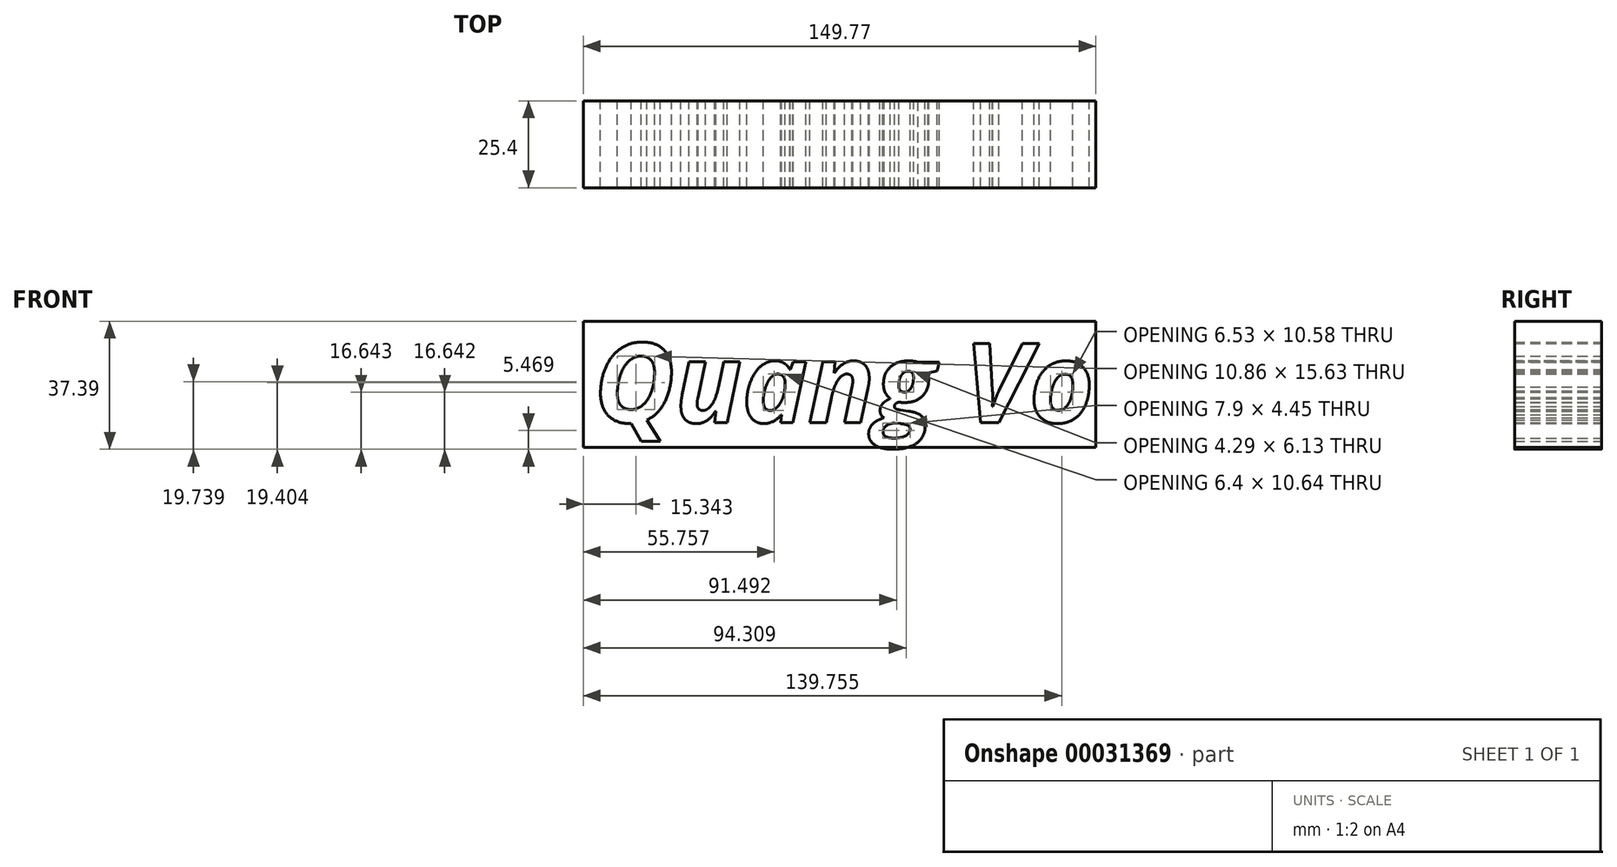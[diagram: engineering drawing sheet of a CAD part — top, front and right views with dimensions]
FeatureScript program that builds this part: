
annotation { "Feature Type Name" : "Feature", "Feature Type Description" : "" }
export const myFeature = defineFeature(function(context is Context, id is Id, definition is map)
    precondition{}
    {
        {
            var Q0;
            Q0=qCreatedBy(makeId("Front.planeOp"),FACE);
            var sketch = newSketch(context, id + "F0", { "sketchPlane" : qUnion([Q0])});
            skText(sketch, "E0", { "text": "Quang Vo ", "fontName": "OpenSans-BoldItalic.ttf"});
            const initialGuessF0  = {"E0": [-0.07156, -0.0073, 1, 0, 0.02335]};
            skSetInitialGuess(sketch, initialGuessF0);
            skSolve(sketch);
        }
        {
            var Q0;
            Q0=qCreatedBy(makeId("Front.planeOp"),FACE);
            var sketch = newSketch(context, id + "F1", { "sketchPlane" : qUnion([Q0])});
            skLineSegment(sketch, "E1.bottom", {"start": v(-74.6, 22.3) * mm, "end": v(75.17, 22.3) * mm});
            skLineSegment(sketch, "E1.top", {"start": v(-74.6, -14.52) * mm, "end": v(75.17, -14.52) * mm});
            skLineSegment(sketch, "E1.left", {"start": v(-74.6, 22.3) * mm, "end": v(-74.6, -14.52) * mm});
            skLineSegment(sketch, "E1.right", {"start": v(75.17, 22.3) * mm, "end": v(75.17, -14.52) * mm});
            skSolve(sketch);
        }
        {
            var Q0;
            Q0=makeQuery(id+"F1.imprint","IMPRINT",FACE,{"disambiguationData":[TD([[makeQuery(id+"F1.imprint","IMPRINT",EDGE,{"derivedFrom":sQuery(id+"F1.wireOp",EDGE,"E1.bottom")}),-1.0]])]});
            extrude(context, id + "F2", {"entities" : qUnion([Q0]), "depth" : 25.4 * mm});
        }
        {
            var Q0;
            Q0 = qSketchRegion(id + "F0", true);
            extrude(context, id + "F3", {"entities" : qUnion([Q0]), "depth" : 25.4 * mm});
        }
    });
